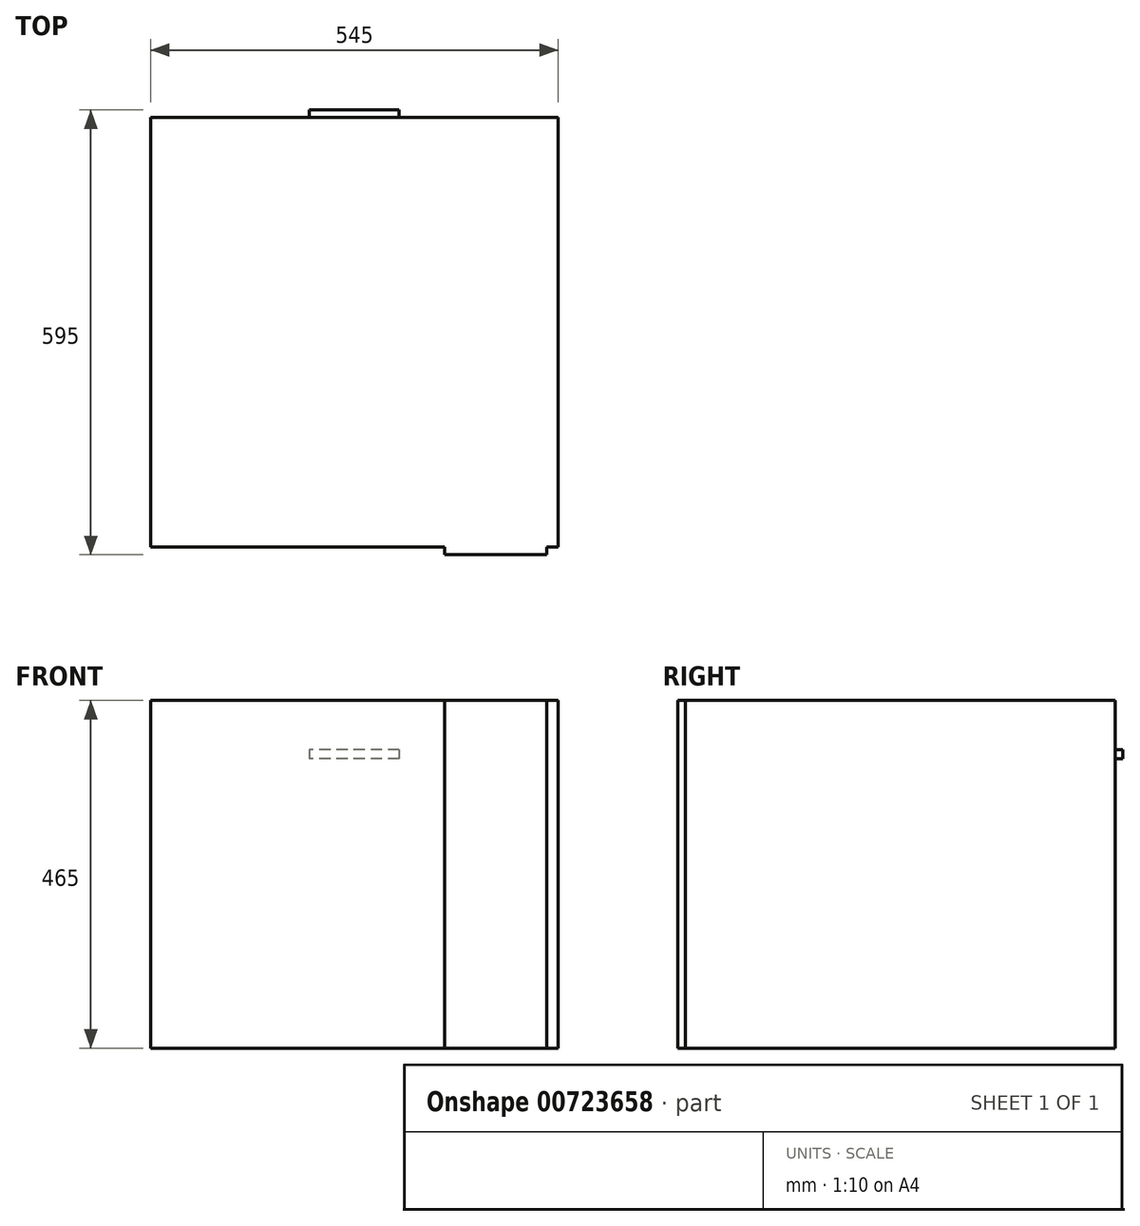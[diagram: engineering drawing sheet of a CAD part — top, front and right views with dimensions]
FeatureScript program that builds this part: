
annotation { "Feature Type Name" : "Feature", "Feature Type Description" : "" }
export const myFeature = defineFeature(function(context is Context, id is Id, definition is map)
    precondition{}
    {
        {
            var Q0;
            Q0=qCreatedBy(makeId("Front.planeOp"),FACE);
            var sketch = newSketch(context, id + "F0", { "sketchPlane" : qUnion([Q0])});
            skLineSegment(sketch, "E0.bottom", {"start": v(-272.5, 232.5) * mm, "end": v(272.5, 232.5) * mm});
            skLineSegment(sketch, "E0.top", {"start": v(-272.5, -232.5) * mm, "end": v(272.5, -232.5) * mm});
            skLineSegment(sketch, "E0.left", {"start": v(-272.5, 232.5) * mm, "end": v(-272.5, -232.5) * mm});
            skLineSegment(sketch, "E0.right", {"start": v(272.5, 232.5) * mm, "end": v(272.5, -232.5) * mm});
            skLineSegment(sketch, "E1", {"start": v(-272.5, 232.5) * mm, "end": v(272.5, -232.5) * mm, "construction": true});
            skSolve(sketch);
        }
        {
            var Q0;
            Q0=makeQuery(id+"F0.imprint","IMPRINT",FACE,{"disambiguationData":[TD([[makeQuery(id+"F0.imprint","IMPRINT",EDGE,{"derivedFrom":sQuery(id+"F0.wireOp",EDGE,"E0.bottom")}),-1.0]])]});
            extrude(context, id + "F1", {"entities" : qUnion([Q0]), "oppositeDirection" : true, "depth" : 575 * mm, "offsetDistance" : 25 * mm});
        }
        {
            var Q0;
            Q0=makeQuery(id+"F1.opExtrude","CAP_FACE",FACE,{"disambiguationData":[OSD([sQuery(id+"F0.wireOp",EDGE,"E0.bottom"),sQuery(id+"F0.wireOp",EDGE,"E0.top"),sQuery(id+"F0.wireOp",EDGE,"E0.left"),sQuery(id+"F0.wireOp",EDGE,"E0.right")])],"isStart":false});
            var sketch = newSketch(context, id + "F2", { "sketchPlane" : qUnion([Q0])});
            skLineSegment(sketch, "E2.bottom", {"start": v(-60, 166.4) * mm, "end": v(60, 166.4) * mm});
            skLineSegment(sketch, "E2.top", {"start": v(-60, 154.4) * mm, "end": v(60, 154.4) * mm});
            skLineSegment(sketch, "E2.left", {"start": v(-60, 166.4) * mm, "end": v(-60, 154.4) * mm});
            skLineSegment(sketch, "E2.right", {"start": v(60, 166.4) * mm, "end": v(60, 154.4) * mm});
            skLineSegment(sketch, "E3", {"start": v(0, 166.4) * mm, "end": v(0, 232.5) * mm, "construction": true});
            skSolve(sketch);
        }
        {
            var Q0;
            Q0 = qSketchRegion(id + "F2", true);
            extrude(context, id + "F3", {"entities" : qUnion([Q0]), "operationType" : NewBodyOperationType.ADD, "depth" : 10 * mm, "offsetDistance" : 25 * mm});
        }
        {
            var Q0;
            Q0=makeQuery(id+"F1.opExtrude","CAP_FACE",FACE,{"disambiguationData":[OSD([sQuery(id+"F0.wireOp",EDGE,"E0.bottom"),sQuery(id+"F0.wireOp",EDGE,"E0.top"),sQuery(id+"F0.wireOp",EDGE,"E0.left"),sQuery(id+"F0.wireOp",EDGE,"E0.right")])],"isStart":true});
            var sketch = newSketch(context, id + "F4", { "sketchPlane" : qUnion([Q0])});
            skLineSegment(sketch, "E4.bottom", {"start": v(120.64, -232.5) * mm, "end": v(257, -232.5) * mm});
            skLineSegment(sketch, "E4.top", {"start": v(120.64, 232.5) * mm, "end": v(257, 232.5) * mm});
            skLineSegment(sketch, "E4.left", {"start": v(120.64, -232.5) * mm, "end": v(120.64, 232.5) * mm});
            skLineSegment(sketch, "E4.right", {"start": v(257, -232.5) * mm, "end": v(257, 232.5) * mm});
            skSolve(sketch);
        }
        {
            var Q0;
            Q0 = qSketchRegion(id + "F4", true);
            extrude(context, id + "F5", {"entities" : qUnion([Q0]), "operationType" : NewBodyOperationType.ADD, "depth" : 10 * mm, "offsetDistance" : 25 * mm});
        }
    });
